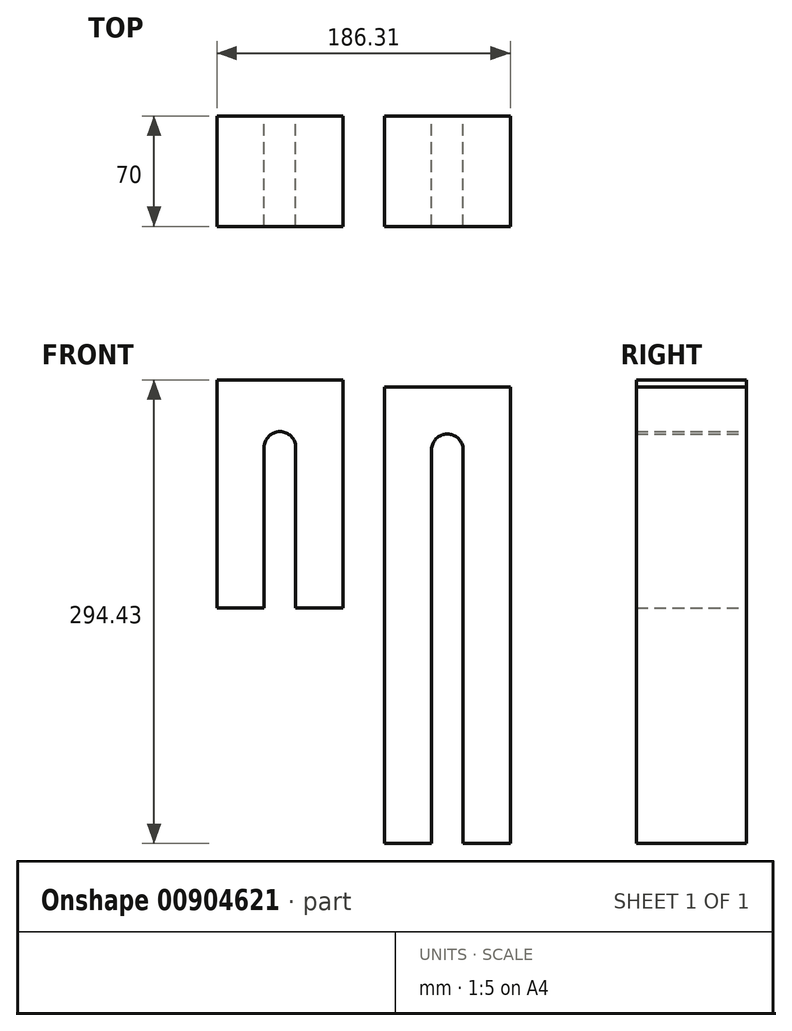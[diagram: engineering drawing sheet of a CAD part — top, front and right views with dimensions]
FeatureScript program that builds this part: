
annotation { "Feature Type Name" : "Feature", "Feature Type Description" : "" }
export const myFeature = defineFeature(function(context is Context, id is Id, definition is map)
    precondition{}
    {
        {
            var Q0;
            Q0=qCreatedBy(makeId("Front.planeOp"),FACE);
            var sketch = newSketch(context, id + "F0", { "sketchPlane" : qUnion([Q0])});
            skLineSegment(sketch, "E0", {"start": v(-79.84, -84.4) * mm, "end": v(-79.84, 60.6) * mm});
            skLineSegment(sketch, "E1", {"start": v(-79.84, 60.6) * mm, "end": v(0.16, 60.6) * mm});
            skLineSegment(sketch, "E2", {"start": v(0.16, 60.6) * mm, "end": v(0.16, -84.4) * mm});
            skLineSegment(sketch, "E3", {"start": v(0.16, -84.4) * mm, "end": v(-29.84, -84.4) * mm});
            skLineSegment(sketch, "E4", {"start": v(-29.84, -84.4) * mm, "end": v(-29.84, 17.7) * mm});
            skLineSegment(sketch, "E5", {"start": v(-39.84, 27.7) * mm, "end": v(-39.84, 27.7) * mm});
            skLineSegment(sketch, "E6", {"start": v(-49.84, 17.7) * mm, "end": v(-49.84, -84.4) * mm});
            skLineSegment(sketch, "E7", {"start": v(-49.84, -84.4) * mm, "end": v(-79.84, -84.4) * mm});
            skPoint(sketch, "E8.visualSharp", {"position": v(-49.84, 27.7) * mm});
            skArc(sketch, "E8.filletArc", {"start": v(-39.84, 27.7) * mm, "mid": v(-46.9, 24.78) * mm, "end": v(-49.84, 17.7) * mm});
            skPoint(sketch, "E9.visualSharp", {"position": v(-29.84, 27.7) * mm});
            skArc(sketch, "E9.filletArc", {"start": v(-29.84, 17.7) * mm, "mid": v(-32.77, 24.78) * mm, "end": v(-39.84, 27.7) * mm});
            skSolve(sketch);
        }
        {
            var Q0;
            Q0 = qSketchRegion(id + "F0", true);
            extrude(context, id + "F1", {"entities" : qUnion([Q0]), "depth" : 70 * mm, "offsetDistance" : 25 * mm});
        }
        {
            var Q0;
            Q0=qCreatedBy(makeId("Front.planeOp"),FACE);
            var sketch = newSketch(context, id + "F2", { "sketchPlane" : qUnion([Q0])});
            skLineSegment(sketch, "E10", {"start": v(26.47, -233.82) * mm, "end": v(26.47, 56.18) * mm});
            skLineSegment(sketch, "E11", {"start": v(26.47, 56.18) * mm, "end": v(106.47, 56.18) * mm});
            skLineSegment(sketch, "E12", {"start": v(106.47, 56.18) * mm, "end": v(106.47, -233.82) * mm});
            skLineSegment(sketch, "E13", {"start": v(106.47, -233.82) * mm, "end": v(76.47, -233.82) * mm});
            skLineSegment(sketch, "E14", {"start": v(76.47, -233.82) * mm, "end": v(76.47, 16.18) * mm});
            skLineSegment(sketch, "E15", {"start": v(66.47, 60.18) * mm, "end": v(66.47, 60.18) * mm});
            skLineSegment(sketch, "E16", {"start": v(56.47, 16.18) * mm, "end": v(56.47, -233.82) * mm});
            skLineSegment(sketch, "E17", {"start": v(56.47, -233.82) * mm, "end": v(26.47, -233.82) * mm});
            skPoint(sketch, "E18.visualSharp", {"position": v(56.47, 26.18) * mm});
            skArc(sketch, "E18.filletArc", {"start": v(66.47, 26.18) * mm, "mid": v(59.4, 23.25) * mm, "end": v(56.47, 16.18) * mm});
            skPoint(sketch, "E19.visualSharp", {"position": v(76.47, 26.18) * mm});
            skArc(sketch, "E19.filletArc", {"start": v(76.47, 16.18) * mm, "mid": v(73.54, 23.25) * mm, "end": v(66.47, 26.18) * mm});
            skSolve(sketch);
        }
        {
            var Q0;
            Q0 = qSketchRegion(id + "F2", true);
            extrude(context, id + "F3", {"entities" : qUnion([Q0]), "depth" : 70 * mm, "offsetDistance" : 25 * mm});
        }
    });
